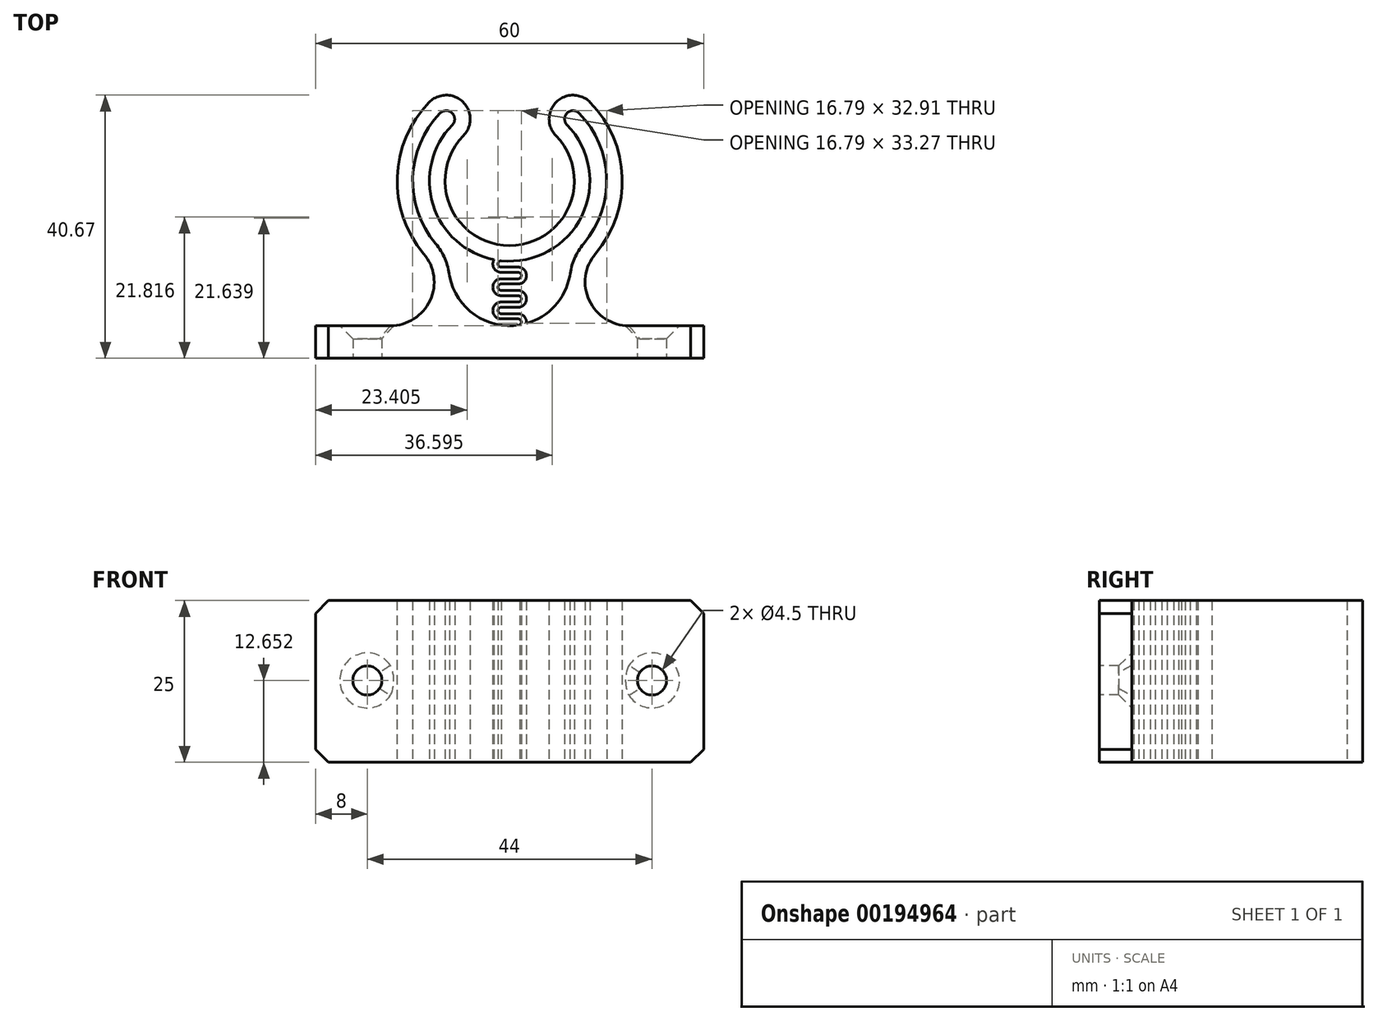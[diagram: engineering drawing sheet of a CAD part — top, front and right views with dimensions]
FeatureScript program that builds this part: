
annotation { "Feature Type Name" : "Feature", "Feature Type Description" : "" }
export const myFeature = defineFeature(function(context is Context, id is Id, definition is map)
    precondition{}
    {
        {
            var Q0;
            Q0=qCreatedBy(makeId("Top.planeOp"),FACE);
            var sketch = newSketch(context, id + "F0", { "sketchPlane" : qUnion([Q0])});
            skCircle(sketch, "E0", {"center": v(0, 0) * mm, "radius": 10 * mm});
            skCircle(sketch, "E1", {"center": v(0, 0) * mm, "radius": 15 * mm});
            skCircle(sketch, "E2.0", {"center": v(0, 0) * mm, "radius": 17.4 * mm});
            skCircle(sketch, "E3.0", {"center": v(0, 0) * mm, "radius": 12.4 * mm});
            skLineSegment(sketch, "E4", {"start": v(0, 0) * mm, "end": v(-11.69, 20.25) * mm, "construction": true});
            skLineSegment(sketch, "E5", {"start": v(-11.69, 20.25) * mm, "end": v(11.69, 20.25) * mm, "construction": true});
            skLineSegment(sketch, "E6", {"start": v(11.69, 20.25) * mm, "end": v(0, 0) * mm, "construction": true});
            skCircle(sketch, "E7", {"center": v(9.8, 9.57) * mm, "radius": 3.7 * mm});
            skCircle(sketch, "E8", {"center": v(-9.8, 9.57) * mm, "radius": 3.7 * mm});
            skCircle(sketch, "E9.0", {"center": v(-9.8, 9.57) * mm, "radius": 1.3 * mm});
            skCircle(sketch, "E10.0", {"center": v(9.8, 9.57) * mm, "radius": 1.3 * mm});
            skLineSegment(sketch, "E11.bottom", {"start": v(-30, -27.4) * mm, "end": v(30, -27.4) * mm});
            skLineSegment(sketch, "E11.top", {"start": v(-30, -22.4) * mm, "end": v(30, -22.4) * mm});
            skLineSegment(sketch, "E11.left", {"start": v(-30, -27.4) * mm, "end": v(-30, -22.4) * mm});
            skLineSegment(sketch, "E11.right", {"start": v(30, -27.4) * mm, "end": v(30, -22.4) * mm});
            skCircle(sketch, "E12", {"center": v(-18.44, -15.63) * mm, "radius": 6.77 * mm});
            skCircle(sketch, "E13", {"center": v(18.44, -15.63) * mm, "radius": 6.77 * mm});
            skCircle(sketch, "E14.0", {"center": v(-18.44, -15.63) * mm, "radius": 9.17 * mm});
            skCircle(sketch, "E15.0", {"center": v(18.44, -15.63) * mm, "radius": 9.17 * mm});
            skCircle(sketch, "E16", {"center": v(0, -12.94) * mm, "radius": 9.46 * mm});
            skSolve(sketch);
        }
        {
            var Q0;
            {var subQ0=sQuery(id+"F0.wireOp",EDGE,"E12");var subQ1=sQuery(id+"F0.wireOp",EDGE,"E2.0");var subQ2=makeQuery(id+"F0.imprint","INTERSECT",VERTEX,{"derivedFrom":[subQ1,subQ0]});Q0=makeQuery(id+"F0.imprint","IMPRINT",FACE,{"disambiguationData":[TD([[makeQuery(id+"F0.imprint","IMPRINT",EDGE,{"disambiguationData":[TD([[subQ2,-1.0]])],"derivedFrom":subQ1}),-1.0]])]});}
            var Q1;
            {var subQ0=sQuery(id+"F0.wireOp",EDGE,"E8");var subQ1=sQuery(id+"F0.wireOp",EDGE,"E1");var subQ2=makeQuery(id+"F0.imprint","INTERSECT",VERTEX,{"disambiguationData":[OD(1.0)],"derivedFrom":[subQ1,subQ0]});Q1=makeQuery(id+"F0.imprint","IMPRINT",FACE,{"disambiguationData":[TD([[makeQuery(id+"F0.imprint","IMPRINT",EDGE,{"disambiguationData":[TD([[subQ2,-1.0]])],"derivedFrom":subQ1}),-1.0]])]});}
            var Q2;
            {var subQ0=sQuery(id+"F0.wireOp",EDGE,"E14.0");var subQ3=sQuery(id+"F0.wireOp",EDGE,"E2.0");var subQ6=makeQuery(id+"F0.imprint","INTERSECT",VERTEX,{"disambiguationData":[OD(0.0)],"derivedFrom":[subQ3,subQ0]});Q2=makeQuery(id+"F0.imprint","IMPRINT",FACE,{"disambiguationData":[TD([[makeQuery(id+"F0.imprint","IMPRINT",EDGE,{"disambiguationData":[TD([[subQ6,-1.0]])],"derivedFrom":subQ3}),1.0]])]});}
            var Q3;
            {var subQ0=sQuery(id+"F0.wireOp",EDGE,"E14.0");var subQ1=sQuery(id+"F0.wireOp",EDGE,"E2.0");var subQ2=makeQuery(id+"F0.imprint","INTERSECT",VERTEX,{"disambiguationData":[OD(1.0)],"derivedFrom":[subQ1,subQ0]});Q3=makeQuery(id+"F0.imprint","IMPRINT",FACE,{"disambiguationData":[TD([[makeQuery(id+"F0.imprint","IMPRINT",EDGE,{"disambiguationData":[TD([[subQ2,-1.0]])],"derivedFrom":subQ1}),-1.0]])]});}
            var Q4;
            {var subQ0=sQuery(id+"F0.wireOp",EDGE,"E16");var subQ1=sQuery(id+"F0.wireOp",EDGE,"E2.0");var subQ2=makeQuery(id+"F0.imprint","INTERSECT",VERTEX,{"disambiguationData":[OD(1.0)],"derivedFrom":[subQ1,subQ0]});Q4=makeQuery(id+"F0.imprint","IMPRINT",FACE,{"disambiguationData":[TD([[makeQuery(id+"F0.imprint","IMPRINT",EDGE,{"disambiguationData":[TD([[subQ2,-1.0]])],"derivedFrom":subQ1}),-1.0]])]});}
            var Q5;
            {var subQ0=sQuery(id+"F0.wireOp",EDGE,"E15.0");var subQ1=sQuery(id+"F0.wireOp",EDGE,"E2.0");var subQ2=makeQuery(id+"F0.imprint","INTERSECT",VERTEX,{"disambiguationData":[OD(1.0)],"derivedFrom":[subQ1,subQ0]});Q5=makeQuery(id+"F0.imprint","IMPRINT",FACE,{"disambiguationData":[TD([[makeQuery(id+"F0.imprint","IMPRINT",EDGE,{"disambiguationData":[TD([[subQ2,-1.0]])],"derivedFrom":subQ1}),-1.0]])]});}
            var Q6;
            {var subQ0=sQuery(id+"F0.wireOp",EDGE,"E15.0");var subQ3=sQuery(id+"F0.wireOp",EDGE,"E2.0");var subQ6=makeQuery(id+"F0.imprint","INTERSECT",VERTEX,{"disambiguationData":[OD(1.0)],"derivedFrom":[subQ3,subQ0]});Q6=makeQuery(id+"F0.imprint","IMPRINT",FACE,{"disambiguationData":[TD([[makeQuery(id+"F0.imprint","IMPRINT",EDGE,{"disambiguationData":[TD([[subQ6,-1.0]])],"derivedFrom":subQ3}),1.0]])]});}
            var Q7;
            {var subQ0=sQuery(id+"F0.wireOp",EDGE,"E7");var subQ1=sQuery(id+"F0.wireOp",EDGE,"E1");var subQ2=makeQuery(id+"F0.imprint","INTERSECT",VERTEX,{"disambiguationData":[OD(0.0)],"derivedFrom":[subQ1,subQ0]});Q7=makeQuery(id+"F0.imprint","IMPRINT",FACE,{"disambiguationData":[TD([[makeQuery(id+"F0.imprint","IMPRINT",EDGE,{"disambiguationData":[TD([[subQ2,1.0]])],"derivedFrom":subQ1}),-1.0]])]});}
            var Q8;
            {var subQ0=sQuery(id+"F0.wireOp",EDGE,"E1");var subQ1=makeQuery(id+"F0.imprint","INTERSECT",VERTEX,{"derivedFrom":[subQ0,sQuery(id+"F0.wireOp",EDGE,"E10.0")]});Q8=makeQuery(id+"F0.imprint","IMPRINT",FACE,{"disambiguationData":[TD([[makeQuery(id+"F0.imprint","IMPRINT",EDGE,{"disambiguationData":[TD([[subQ1,1.0]])],"derivedFrom":subQ0}),-1.0]])]});}
            var Q9;
            {var subQ0=sQuery(id+"F0.wireOp",EDGE,"E10.0");var subQ1=sQuery(id+"F0.wireOp",EDGE,"E1");var subQ2=makeQuery(id+"F0.imprint","INTERSECT",VERTEX,{"derivedFrom":[subQ1,subQ0]});Q9=makeQuery(id+"F0.imprint","IMPRINT",FACE,{"disambiguationData":[TD([[makeQuery(id+"F0.imprint","IMPRINT",EDGE,{"disambiguationData":[TD([[subQ2,-1.0]])],"derivedFrom":subQ1}),1.0]])]});}
            var Q10;
            {var subQ0=sQuery(id+"F0.wireOp",EDGE,"E3.0");var subQ1=makeQuery(id+"F0.imprint","INTERSECT",VERTEX,{"derivedFrom":[subQ0,sQuery(id+"F0.wireOp",EDGE,"E10.0")]});Q10=makeQuery(id+"F0.imprint","IMPRINT",FACE,{"disambiguationData":[TD([[makeQuery(id+"F0.imprint","IMPRINT",EDGE,{"disambiguationData":[TD([[subQ1,1.0]])],"derivedFrom":subQ0}),1.0]])]});}
            var Q11;
            {var subQ0=sQuery(id+"F0.wireOp",EDGE,"E7");var subQ1=sQuery(id+"F0.wireOp",EDGE,"E0");var subQ2=makeQuery(id+"F0.imprint","INTERSECT",VERTEX,{"derivedFrom":[subQ1,subQ0]});Q11=makeQuery(id+"F0.imprint","IMPRINT",FACE,{"disambiguationData":[TD([[makeQuery(id+"F0.imprint","IMPRINT",EDGE,{"disambiguationData":[TD([[subQ2,1.0]])],"derivedFrom":subQ1}),-1.0]])]});}
            var Q12;
            {var subQ0=sQuery(id+"F0.wireOp",EDGE,"E16");var subQ1=sQuery(id+"F0.wireOp",EDGE,"E0");var subQ2=makeQuery(id+"F0.imprint","INTERSECT",VERTEX,{"disambiguationData":[OD(0.0)],"derivedFrom":[subQ1,subQ0]});Q12=makeQuery(id+"F0.imprint","IMPRINT",FACE,{"disambiguationData":[TD([[makeQuery(id+"F0.imprint","IMPRINT",EDGE,{"disambiguationData":[TD([[subQ2,-1.0]])],"derivedFrom":subQ1}),-1.0]])]});}
            var Q13;
            {var subQ0=sQuery(id+"F0.wireOp",EDGE,"E8");var subQ1=sQuery(id+"F0.wireOp",EDGE,"E0");var subQ2=makeQuery(id+"F0.imprint","INTERSECT",VERTEX,{"derivedFrom":[subQ1,subQ0]});Q13=makeQuery(id+"F0.imprint","IMPRINT",FACE,{"disambiguationData":[TD([[makeQuery(id+"F0.imprint","IMPRINT",EDGE,{"disambiguationData":[TD([[subQ2,-1.0]])],"derivedFrom":subQ1}),-1.0]])]});}
            var Q14;
            {var subQ0=sQuery(id+"F0.wireOp",EDGE,"E8");var subQ1=sQuery(id+"F0.wireOp",EDGE,"E3.0");var subQ2=makeQuery(id+"F0.imprint","INTERSECT",VERTEX,{"disambiguationData":[OD(0.0)],"derivedFrom":[subQ1,subQ0]});Q14=makeQuery(id+"F0.imprint","IMPRINT",FACE,{"disambiguationData":[TD([[makeQuery(id+"F0.imprint","IMPRINT",EDGE,{"disambiguationData":[TD([[subQ2,-1.0]])],"derivedFrom":subQ1}),1.0]])]});}
            var Q15;
            {var subQ0=sQuery(id+"F0.wireOp",EDGE,"E8");var subQ1=sQuery(id+"F0.wireOp",EDGE,"E1");var subQ2=makeQuery(id+"F0.imprint","INTERSECT",VERTEX,{"disambiguationData":[OD(0.0)],"derivedFrom":[subQ1,subQ0]});Q15=makeQuery(id+"F0.imprint","IMPRINT",FACE,{"disambiguationData":[TD([[makeQuery(id+"F0.imprint","IMPRINT",EDGE,{"disambiguationData":[TD([[subQ2,-1.0]])],"derivedFrom":subQ1}),1.0]])]});}
            var Q16;
            {var subQ0=sQuery(id+"F0.wireOp",EDGE,"E8");var subQ1=sQuery(id+"F0.wireOp",EDGE,"E1");var subQ2=makeQuery(id+"F0.imprint","INTERSECT",VERTEX,{"disambiguationData":[OD(0.0)],"derivedFrom":[subQ1,subQ0]});Q16=makeQuery(id+"F0.imprint","IMPRINT",FACE,{"disambiguationData":[TD([[makeQuery(id+"F0.imprint","IMPRINT",EDGE,{"disambiguationData":[TD([[subQ2,-1.0]])],"derivedFrom":subQ1}),-1.0]])]});}
            var Q17;
            Q17=makeQuery(id+"F0.imprint","IMPRINT",FACE,{"disambiguationData":[TD([[makeQuery(id+"F0.imprint","IMPRINT",EDGE,{"derivedFrom":sQuery(id+"F0.wireOp",EDGE,"E11.bottom")}),1.0]])]});
            var Q18;
            {var subQ0=sQuery(id+"F0.wireOp",EDGE,"E14.0");var subQ1=sQuery(id+"F0.wireOp",EDGE,"E11.top");var subQ2=makeQuery(id+"F0.imprint","INTERSECT",VERTEX,{"disambiguationData":[OD(0.0)],"derivedFrom":[subQ1,subQ0]});Q18=makeQuery(id+"F0.imprint","IMPRINT",FACE,{"disambiguationData":[TD([[makeQuery(id+"F0.imprint","IMPRINT",EDGE,{"disambiguationData":[TD([[subQ2,-1.0]])],"derivedFrom":subQ1}),-1.0]])]});}
            var Q19;
            {var subQ0=sQuery(id+"F0.wireOp",EDGE,"E15.0");var subQ1=sQuery(id+"F0.wireOp",EDGE,"E11.top");var subQ2=makeQuery(id+"F0.imprint","INTERSECT",VERTEX,{"disambiguationData":[OD(1.0)],"derivedFrom":[subQ1,subQ0]});Q19=makeQuery(id+"F0.imprint","IMPRINT",FACE,{"disambiguationData":[TD([[makeQuery(id+"F0.imprint","IMPRINT",EDGE,{"disambiguationData":[TD([[subQ2,-1.0]])],"derivedFrom":subQ1}),-1.0]])]});}
            extrude(context, id + "F1", {"entities" : qUnion([Q0, Q1, Q2, Q3, Q4, Q5, Q6, Q7, Q8, Q9, Q10, Q11, Q12, Q13, Q14, Q15, Q16, Q17, Q18, Q19]), "depth" : 25 * mm});
        }
        {
            var Q0;
            Q0=makeQuery(id+"F1.opExtrude","SWEPT_FACE",FACE,{"disambiguationData":[OSD([sQuery(id+"F0.wireOp",EDGE,"E11.bottom")])]});
            var sketch = newSketch(context, id + "F2", { "sketchPlane" : qUnion([Q0])});
            skCircle(sketch, "E17", {"center": v(-22, 12.65) * mm, "radius": 2.25 * mm});
            skCircle(sketch, "E18", {"center": v(22, 12.65) * mm, "radius": 2.25 * mm});
            skSolve(sketch);
        }
        {
            var Q0;
            Q0=makeQuery(id+"F2.imprint","IMPRINT",FACE,{"disambiguationData":[TD([[makeQuery(id+"F2.imprint","IMPRINT",EDGE,{"derivedFrom":sQuery(id+"F2.wireOp",EDGE,"E17")}),1.0]])]});
            var Q1;
            Q1=makeQuery(id+"F2.imprint","IMPRINT",FACE,{"disambiguationData":[TD([[makeQuery(id+"F2.imprint","IMPRINT",EDGE,{"derivedFrom":sQuery(id+"F2.wireOp",EDGE,"E18")}),1.0]])]});
            extrude(context, id + "F3", {"entities" : qUnion([Q0, Q1]), "operationType" : NewBodyOperationType.REMOVE, "oppositeDirection" : true, "depth" : 25 * mm});
        }
        {
            var Q0;
            {var subQ0=sQuery(id+"F0.wireOp",EDGE,"E11.top");var subQ1=makeQuery(id+"F0.imprint","INTERSECT",VERTEX,{"disambiguationData":[OD(0.0)],"derivedFrom":[subQ0,sQuery(id+"F0.wireOp",EDGE,"E15.0")]});Q0=makeQuery(id+"F3.boolean.opBoolean","INTERSECT",EDGE,{"derivedFrom":[makeQuery(id+"F1.opExtrude","SWEPT_FACE",FACE,{"disambiguationData":[OSD([subQ0]),TDD([makeQuery(id+"F0.imprint","IMPRINT",EDGE,{"disambiguationData":[TD([[subQ1,1.0]])],"derivedFrom":subQ0}),makeQuery(id+"F0.imprint","IMPRINT",EDGE,{"disambiguationData":[TD([[makeQuery(id+"F0.imprint","INTERSECT",VERTEX,{"derivedFrom":[subQ0,sQuery(id+"F0.wireOp",EDGE,"E11.right")]}),1.0]])],"derivedFrom":subQ0})])]}),makeQuery(id+"F3.opExtrude","SWEPT_FACE",FACE,{"disambiguationData":[OSD([sQuery(id+"F2.wireOp",EDGE,"E18")])]})]});}
            var Q1;
            {var subQ0=sQuery(id+"F0.wireOp",EDGE,"E11.top");var subQ1=makeQuery(id+"F0.imprint","INTERSECT",VERTEX,{"disambiguationData":[OD(0.0)],"derivedFrom":[subQ0,sQuery(id+"F0.wireOp",EDGE,"E14.0")]});Q1=makeQuery(id+"F3.boolean.opBoolean","INTERSECT",EDGE,{"derivedFrom":[makeQuery(id+"F1.opExtrude","SWEPT_FACE",FACE,{"disambiguationData":[OSD([subQ0]),TDD([makeQuery(id+"F0.imprint","IMPRINT",EDGE,{"disambiguationData":[TD([[makeQuery(id+"F0.imprint","INTERSECT",VERTEX,{"derivedFrom":[subQ0,sQuery(id+"F0.wireOp",EDGE,"E11.left")]}),-1.0]])],"derivedFrom":subQ0}),makeQuery(id+"F0.imprint","IMPRINT",EDGE,{"disambiguationData":[TD([[subQ1,-1.0]])],"derivedFrom":subQ0})])]}),makeQuery(id+"F3.opExtrude","SWEPT_FACE",FACE,{"disambiguationData":[OSD([sQuery(id+"F2.wireOp",EDGE,"E17")])]})]});}
            chamfer(context, id + "F4", {"entities" : qUnion([Q0, Q1]), "width" : 2 * mm, "tangentPropagation" : true});
        }
        {
            var Q0;
            Q0=makeQuery(id+"F1.opExtrude","CAP_EDGE",EDGE,{"disambiguationData":[OSD([sQuery(id+"F0.wireOp",EDGE,"E11.right")])],"isStart":true});
            var Q1;
            Q1=makeQuery(id+"F1.opExtrude","CAP_EDGE",EDGE,{"disambiguationData":[OSD([sQuery(id+"F0.wireOp",EDGE,"E11.left")])],"isStart":true});
            var Q2;
            Q2=makeQuery(id+"F1.opExtrude","CAP_EDGE",EDGE,{"disambiguationData":[OSD([sQuery(id+"F0.wireOp",EDGE,"E11.left")])],"isStart":false});
            var Q3;
            Q3=makeQuery(id+"F1.opExtrude","CAP_EDGE",EDGE,{"disambiguationData":[OSD([sQuery(id+"F0.wireOp",EDGE,"E11.right")])],"isStart":false});
            chamfer(context, id + "F5", {"entities" : qUnion([Q0, Q1, Q2, Q3]), "width" : 2 * mm, "tangentPropagation" : true});
        }
        {
            var Q0;
            Q0=qCreatedBy(makeId("Top.planeOp"),FACE);
            var sketch = newSketch(context, id + "F6", { "sketchPlane" : qUnion([Q0])});
            skCircle(sketch, "E19", {"center": v(-1.3, -12.83) * mm, "radius": 0.5 * mm});
            skCircle(sketch, "E20", {"center": v(1.3, -14.63) * mm, "radius": 0.5 * mm});
            skCircle(sketch, "E21", {"center": v(-1.3, -12.83) * mm, "radius": 1.3 * mm});
            skCircle(sketch, "E22", {"center": v(1.3, -14.63) * mm, "radius": 1.3 * mm});
            skLineSegment(sketch, "E23", {"start": v(-1.3, -13.33) * mm, "end": v(1.3, -13.33) * mm, "construction": true});
            skLineSegment(sketch, "E24", {"start": v(1.3, -15.13) * mm, "end": v(-4.06, -15.13) * mm, "construction": true});
            skCircle(sketch, "E25.0.1.0", {"center": v(-1.3, -16.43) * mm, "radius": 1.3 * mm});
            skCircle(sketch, "E25.0.1.1", {"center": v(-1.3, -16.43) * mm, "radius": 0.5 * mm});
            skCircle(sketch, "E25.0.1.2", {"center": v(1.3, -18.23) * mm, "radius": 1.3 * mm});
            skCircle(sketch, "E25.0.1.3", {"center": v(1.3, -18.23) * mm, "radius": 0.5 * mm});
            skCircle(sketch, "E25.0.2.0", {"center": v(-1.3, -20.03) * mm, "radius": 1.3 * mm});
            skCircle(sketch, "E25.0.2.1", {"center": v(-1.3, -20.03) * mm, "radius": 0.5 * mm});
            skCircle(sketch, "E25.0.2.2", {"center": v(1.3, -21.83) * mm, "radius": 1.3 * mm});
            skCircle(sketch, "E25.0.2.3", {"center": v(1.3, -21.83) * mm, "radius": 0.5 * mm});
            skLineSegment(sketch, "E25.direction1", {"start": v(-1.3, -12.83) * mm, "end": v(23.7, -12.83) * mm, "construction": true});
            skLineSegment(sketch, "E25.direction2", {"start": v(-1.3, -12.83) * mm, "end": v(-1.3, -16.43) * mm, "construction": true});
            skLineSegment(sketch, "E26", {"start": v(-1.3, -13.33) * mm, "end": v(1.3, -13.33) * mm});
            skLineSegment(sketch, "E27", {"start": v(1.3, -15.13) * mm, "end": v(-1.3, -15.13) * mm});
            skPoint(sketch, "E28", {"position": v(-1.3, -17.73) * mm});
            skPoint(sketch, "E29", {"position": v(-1.3, -16.93) * mm});
            skPoint(sketch, "E30", {"position": v(-1.3, -18.73) * mm});
            skPoint(sketch, "E31", {"position": v(-1.3, -19.53) * mm});
            skPoint(sketch, "E32", {"position": v(-1.3, -20.53) * mm});
            skPoint(sketch, "E33", {"position": v(-1.3, -21.33) * mm});
            skPoint(sketch, "E34", {"position": v(-1.3, -15.93) * mm});
            skLineSegment(sketch, "E35", {"start": v(1.3, -13.33) * mm, "end": v(1.3, -22.04) * mm, "construction": true});
            skPoint(sketch, "E36", {"position": v(1.3, -14.13) * mm});
            skPoint(sketch, "E37", {"position": v(-1.3, -14.13) * mm});
            skPoint(sketch, "E38", {"position": v(1.3, -15.93) * mm});
            skPoint(sketch, "E39", {"position": v(1.3, -16.93) * mm});
            skPoint(sketch, "E40", {"position": v(1.3, -17.73) * mm});
            skPoint(sketch, "E41", {"position": v(1.3, -18.73) * mm});
            skPoint(sketch, "E42", {"position": v(1.3, -19.53) * mm});
            skPoint(sketch, "E43", {"position": v(1.3, -20.53) * mm});
            skPoint(sketch, "E44", {"position": v(1.3, -21.33) * mm});
            skLineSegment(sketch, "E45", {"start": v(-1.3, -21.33) * mm, "end": v(1.3, -21.33) * mm});
            skLineSegment(sketch, "E46", {"start": v(1.3, -20.53) * mm, "end": v(-1.3, -20.53) * mm});
            skLineSegment(sketch, "E47", {"start": v(-1.3, -19.53) * mm, "end": v(1.3, -19.53) * mm});
            skLineSegment(sketch, "E48", {"start": v(-1.3, -18.73) * mm, "end": v(1.3, -18.73) * mm});
            skLineSegment(sketch, "E49", {"start": v(1.3, -17.73) * mm, "end": v(-1.3, -17.73) * mm});
            skLineSegment(sketch, "E50", {"start": v(-1.3, -16.93) * mm, "end": v(1.3, -16.93) * mm});
            skLineSegment(sketch, "E51", {"start": v(-1.3, -15.93) * mm, "end": v(1.3, -15.93) * mm});
            skLineSegment(sketch, "E52", {"start": v(1.3, -14.13) * mm, "end": v(-1.3, -14.13) * mm});
            skLineSegment(sketch, "E53", {"start": v(-1.3, -12.33) * mm, "end": v(-1.3, -11.53) * mm});
            skLineSegment(sketch, "E54", {"start": v(1.34, -22.33) * mm, "end": v(1.34, -23.13) * mm});
            skSolve(sketch);
        }
        {
            var Q0;
            {var subQ5=sQuery(id+"F6.wireOp",EDGE,"E25.0.2.0");var subQ8=makeQuery(id+"F6.imprint","INTERSECT",VERTEX,{"derivedFrom":[subQ5,sQuery(id+"F6.wireOp",EDGE,"E48")]});Q0=makeQuery(id+"F6.imprint","IMPRINT",FACE,{"disambiguationData":[TD([[makeQuery(id+"F6.imprint","IMPRINT",EDGE,{"disambiguationData":[TD([[subQ8,1.0]])],"derivedFrom":subQ5}),1.0]])]});}
            var Q1;
            {var subQ0=sQuery(id+"F6.wireOp",EDGE,"E45");var subQ1=sQuery(id+"F6.wireOp",EDGE,"E25.0.2.0");var subQ2=makeQuery(id+"F6.imprint","INTERSECT",VERTEX,{"derivedFrom":[subQ1,subQ0]});Q1=makeQuery(id+"F6.imprint","IMPRINT",FACE,{"disambiguationData":[TD([[makeQuery(id+"F6.imprint","IMPRINT",EDGE,{"disambiguationData":[TD([[subQ2,-1.0]])],"derivedFrom":subQ1}),-1.0]])]});}
            var Q2;
            {var subQ3=sQuery(id+"F6.wireOp",EDGE,"E54");Q2=makeQuery(id+"F6.imprint","IMPRINT",FACE,{"disambiguationData":[TD([[makeQuery(id+"F6.imprint","IMPRINT",EDGE,{"derivedFrom":subQ3}),1.0]])]});}
            var Q3;
            {var subQ0=sQuery(id+"F6.wireOp",EDGE,"E47");var subQ1=sQuery(id+"F6.wireOp",EDGE,"E25.0.1.2");var subQ2=makeQuery(id+"F6.imprint","INTERSECT",VERTEX,{"derivedFrom":[subQ1,subQ0]});Q3=makeQuery(id+"F6.imprint","IMPRINT",FACE,{"disambiguationData":[TD([[makeQuery(id+"F6.imprint","IMPRINT",EDGE,{"disambiguationData":[TD([[subQ2,1.0]])],"derivedFrom":subQ1}),-1.0]])]});}
            var Q4;
            {var subQ0=sQuery(id+"F6.wireOp",EDGE,"E25.0.1.2");var subQ2=makeQuery(id+"F6.imprint","INTERSECT",VERTEX,{"derivedFrom":[subQ0,sQuery(id+"F6.wireOp",EDGE,"E50")]});Q4=makeQuery(id+"F6.imprint","IMPRINT",FACE,{"disambiguationData":[TD([[makeQuery(id+"F6.imprint","IMPRINT",EDGE,{"disambiguationData":[TD([[subQ2,-1.0]])],"derivedFrom":subQ0}),1.0]])]});}
            var Q5;
            {var subQ0=sQuery(id+"F6.wireOp",EDGE,"E49");var subQ1=sQuery(id+"F6.wireOp",EDGE,"E25.0.1.0");var subQ2=makeQuery(id+"F6.imprint","INTERSECT",VERTEX,{"derivedFrom":[subQ1,subQ0]});Q5=makeQuery(id+"F6.imprint","IMPRINT",FACE,{"disambiguationData":[TD([[makeQuery(id+"F6.imprint","IMPRINT",EDGE,{"disambiguationData":[TD([[subQ2,-1.0]])],"derivedFrom":subQ1}),-1.0]])]});}
            var Q6;
            {var subQ5=sQuery(id+"F6.wireOp",EDGE,"E25.0.1.0");var subQ8=makeQuery(id+"F6.imprint","INTERSECT",VERTEX,{"derivedFrom":[subQ5,sQuery(id+"F6.wireOp",EDGE,"E27")]});Q6=makeQuery(id+"F6.imprint","IMPRINT",FACE,{"disambiguationData":[TD([[makeQuery(id+"F6.imprint","IMPRINT",EDGE,{"disambiguationData":[TD([[subQ8,1.0]])],"derivedFrom":subQ5}),1.0]])]});}
            var Q7;
            {var subQ0=sQuery(id+"F6.wireOp",EDGE,"E51");var subQ1=sQuery(id+"F6.wireOp",EDGE,"E22");var subQ2=makeQuery(id+"F6.imprint","INTERSECT",VERTEX,{"derivedFrom":[subQ1,subQ0]});Q7=makeQuery(id+"F6.imprint","IMPRINT",FACE,{"disambiguationData":[TD([[makeQuery(id+"F6.imprint","IMPRINT",EDGE,{"disambiguationData":[TD([[subQ2,1.0]])],"derivedFrom":subQ1}),-1.0]])]});}
            var Q8;
            {var subQ3=sQuery(id+"F6.wireOp",EDGE,"E27");var subQ7=sQuery(id+"F6.wireOp",EDGE,"E20");var subQ8=makeQuery(id+"F6.imprint","INTERSECT",VERTEX,{"derivedFrom":[subQ7,subQ3]});Q8=makeQuery(id+"F6.imprint","IMPRINT",FACE,{"disambiguationData":[TD([[makeQuery(id+"F6.imprint","IMPRINT",EDGE,{"disambiguationData":[TD([[subQ8,-1.0]])],"derivedFrom":subQ7}),-1.0]])]});}
            var Q9;
            {var subQ0=sQuery(id+"F6.wireOp",EDGE,"E52");var subQ1=sQuery(id+"F6.wireOp",EDGE,"E21");var subQ2=makeQuery(id+"F6.imprint","INTERSECT",VERTEX,{"derivedFrom":[subQ1,subQ0]});Q9=makeQuery(id+"F6.imprint","IMPRINT",FACE,{"disambiguationData":[TD([[makeQuery(id+"F6.imprint","IMPRINT",EDGE,{"disambiguationData":[TD([[subQ2,-1.0]])],"derivedFrom":subQ1}),-1.0]])]});}
            var Q10;
            {var subQ6=sQuery(id+"F6.wireOp",EDGE,"E53");Q10=makeQuery(id+"F6.imprint","IMPRINT",FACE,{"disambiguationData":[TD([[makeQuery(id+"F6.imprint","IMPRINT",EDGE,{"derivedFrom":subQ6}),1.0]])]});}
            var Q11;
            Q11=makeQuery(id+"F1.opExtrude","CAP_FACE",FACE,{"disambiguationData":[OSD([sQuery(id+"F0.wireOp",EDGE,"E0"),sQuery(id+"F0.wireOp",EDGE,"E1"),sQuery(id+"F0.wireOp",EDGE,"E2.0"),sQuery(id+"F0.wireOp",EDGE,"E3.0"),sQuery(id+"F0.wireOp",EDGE,"E7"),sQuery(id+"F0.wireOp",EDGE,"E8"),sQuery(id+"F0.wireOp",EDGE,"E9.0"),sQuery(id+"F0.wireOp",EDGE,"E10.0"),sQuery(id+"F0.wireOp",EDGE,"E11.bottom"),sQuery(id+"F0.wireOp",EDGE,"E11.top"),sQuery(id+"F0.wireOp",EDGE,"E11.left"),sQuery(id+"F0.wireOp",EDGE,"E11.right"),sQuery(id+"F0.wireOp",EDGE,"E12"),sQuery(id+"F0.wireOp",EDGE,"E13"),sQuery(id+"F0.wireOp",EDGE,"E14.0"),sQuery(id+"F0.wireOp",EDGE,"E15.0"),sQuery(id+"F0.wireOp",EDGE,"E16")])],"isStart":false});
            extrude(context, id + "F7", {"entities" : qUnion([Q0, Q1, Q2, Q3, Q4, Q5, Q6, Q7, Q8, Q9, Q10]), "operationType" : NewBodyOperationType.ADD, "endBound" : BoundingType.UP_TO_SURFACE, "endBoundEntityFace" : qUnion([Q11]), "depth" : 25 * mm});
        }
    });
